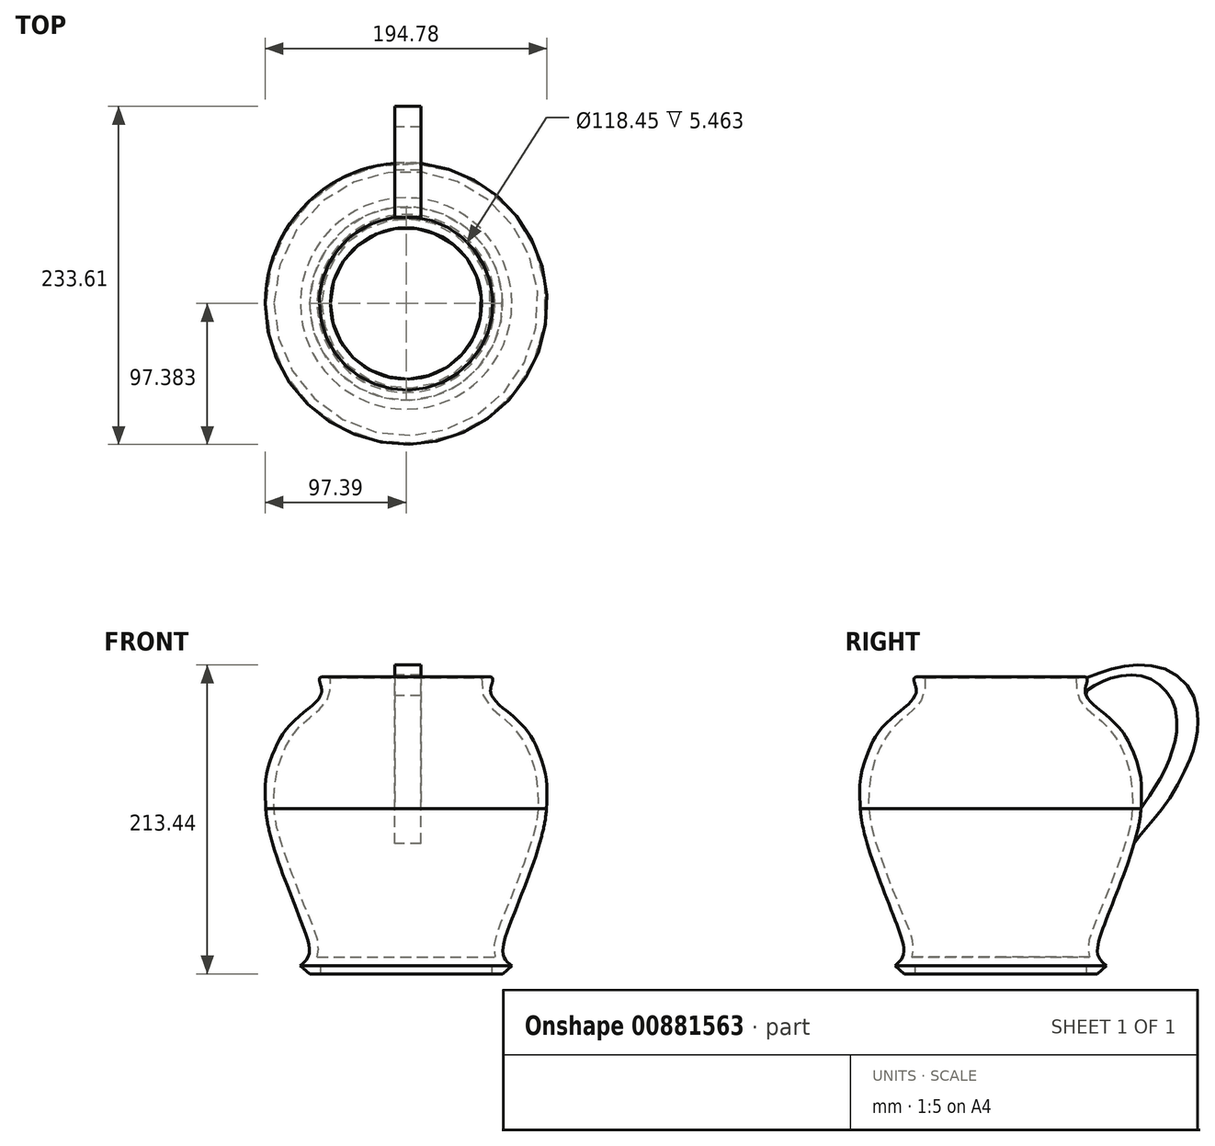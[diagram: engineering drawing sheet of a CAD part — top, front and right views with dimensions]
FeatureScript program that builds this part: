
annotation { "Feature Type Name" : "Feature", "Feature Type Description" : "" }
export const myFeature = defineFeature(function(context is Context, id is Id, definition is map)
    precondition{}
    {
        {
            var Q0;
            Q0=qCreatedBy(makeId("Right.planeOp"),FACE);
            var sketch = newSketch(context, id + "F0", { "sketchPlane" : qUnion([Q0])});
            skLineSegment(sketch, "E0", {"start": v(21, -90.01) * mm, "end": v(21, 114.99) * mm});
            skLineSegment(sketch, "E1", {"start": v(21, -78.5) * mm, "end": v(82.52, -78.5) * mm});
            skLineSegment(sketch, "E2", {"start": v(21, -84.55) * mm, "end": v(80.23, -84.55) * mm});
            skLineSegment(sketch, "E3", {"start": v(80.23, -84.55) * mm, "end": v(80.23, -90.01) * mm});
            skLineSegment(sketch, "E4", {"start": v(80.23, -90.01) * mm, "end": v(87.7, -90.01) * mm});
            skLineSegment(sketch, "E5", {"start": v(87.7, -90.01) * mm, "end": v(94.08, -84.43) * mm});
            skFitSpline(sketch, "E6", {"points": [v(82.52, -78.5) * mm, v(81.64, -74.25) * mm, v(81.95, -67.69) * mm, v(84.48, -59.55) * mm, v(88.62, -49.21) * mm, v(95.1, -33.23) * mm, v(101.8, -15.16) * mm, v(108.67, 4.78) * mm, v(111.86, 19.84) * mm, v(112.27, 30.65) * mm, v(111.12, 44.97) * mm, v(107.42, 59.27) * mm, v(101.35, 71.94) * mm, v(94.22, 81.28) * mm, v(85.7, 88.72) * mm, v(77.6, 96.36) * mm, v(73.85, 103.6) * mm, v(73.28, 114.6) * mm], "startDerivative": vector(-29.85, 113.51) * mm, "endDerivative": vector(3.8, 206.97) * mm});
            skFitSpline(sketch, "E7", {"points": [v(94.08, -84.43) * mm, v(89.53, -79.86) * mm, v(87.84, -73.83) * mm, v(90.13, -63.11) * mm, v(96.16, -47.09) * mm, v(102.34, -31.05) * mm, v(107.8, -16.74) * mm, v(113.24, 0) * mm, v(117.16, 16.62) * mm, v(118.13, 27.14) * mm, v(118.26, 40.74) * mm, v(115.83, 54.5) * mm, v(109.82, 69.46) * mm, v(103.55, 79.43) * mm, v(92.49, 90.01) * mm, v(84.6, 96.46) * mm, v(80.19, 102.2) * mm, v(79.6, 107.78) * mm, v(80.6, 114.6) * mm, v(73.28, 114.6) * mm, v(69.42, 114.6) * mm, v(69.28, 114.6) * mm], "startDerivative": vector(-134.88, 112.2) * mm, "endDerivative": vector(-18, -1) * mm});
            skFitSpline(sketch, "E8", {"points": [v(113.24, 0) * mm, v(118.25, 6.85) * mm, v(127.82, 18.08) * mm, v(140.2, 35.32) * mm, v(151.18, 56.76) * mm, v(154.55, 66.35) * mm, v(156.68, 76.37) * mm, v(156.98, 90.03) * mm, v(152.29, 105.83) * mm, v(137.56, 119.41) * mm, v(117.06, 123.43) * mm, v(98.48, 120.95) * mm, v(80.6, 114.6) * mm], "startDerivative": vector(74.69, 108.6) * mm, "endDerivative": vector(-180.14, -73.73) * mm});
            skFitSpline(sketch, "E9", {"points": [v(80.19, 102.2) * mm, v(80.19, 105.26) * mm, v(88.07, 110.54) * mm, v(95.23, 113.65) * mm, v(107.27, 116.35) * mm, v(118.5, 115.81) * mm, v(129.04, 111.21) * mm, v(136.75, 103.64) * mm, v(141.49, 93.5) * mm, v(142.76, 78.66) * mm, v(140.62, 67.61) * mm, v(137.79, 58.5) * mm, v(132.62, 47.14) * mm, v(126.04, 36.4) * mm, v(120.87, 28.6) * mm, v(117.97, 24.12) * mm, v(117.97, 24.07) * mm], "startDerivative": vector(-36.79, 139.84) * mm, "endDerivative": vector(2.08, -6.5) * mm});
            skSolve(sketch);
        }
        {
            var Q0;
            {var subQ9=sQuery(id+"F0.wireOp",EDGE,"E1");Q0=makeQuery(id+"F0.imprint","IMPRINT",FACE,{"disambiguationData":[TD([[makeQuery(id+"F0.imprint","IMPRINT",EDGE,{"derivedFrom":subQ9}),-1.0]])]});}
            var Q1;
            Q1=sQuery(id+"F0.wireOp",EDGE,"E0");
            revolve(context, id + "F1", {"surfaceOperationType" : NewSurfaceOperationType.NEW, "entities" : qUnion([Q0]), "axis" : qUnion([Q1]), "revolveType" : RevolveType.FULL});
        }
        {
            var Q0;
            {var subQ0=sQuery(id+"F0.wireOp",EDGE,"E8");Q0=makeQuery(id+"F0.imprint","IMPRINT",FACE,{"disambiguationData":[TD([[makeQuery(id+"F0.imprint","IMPRINT",EDGE,{"derivedFrom":subQ0}),1.0]])]});}
            extrude(context, id + "F2", {"entities" : qUnion([Q0]), "depth" : 10.4 * mm, "offsetDistance" : 25 * mm, "hasSecondDirection" : true, "secondDirectionOppositeDirection" : true, "secondDirectionDepth" : 7.8 * mm});
        }
    });
